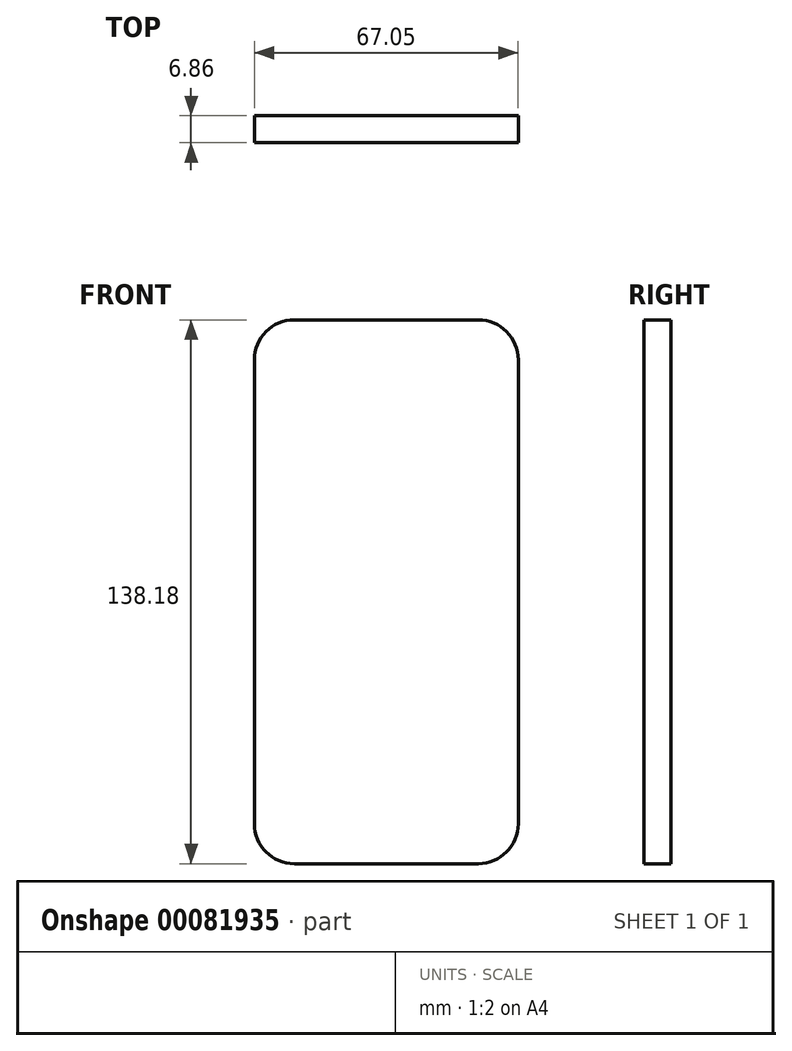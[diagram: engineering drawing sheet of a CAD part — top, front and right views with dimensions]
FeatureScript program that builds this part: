
annotation { "Feature Type Name" : "Feature", "Feature Type Description" : "" }
export const myFeature = defineFeature(function(context is Context, id is Id, definition is map)
    precondition{}
    {
        {
            var Q0;
            Q0=qCreatedBy(makeId("Front.planeOp"),FACE);
            var sketch = newSketch(context, id + "F0", { "sketchPlane" : qUnion([Q0])});
            skLineSegment(sketch, "E0.bottom", {"start": v(-37.54, 72.42) * mm, "end": v(29.51, 72.42) * mm});
            skLineSegment(sketch, "E0.top", {"start": v(-37.54, -65.76) * mm, "end": v(29.51, -65.76) * mm});
            skLineSegment(sketch, "E0.left", {"start": v(-37.54, 72.42) * mm, "end": v(-37.54, -65.76) * mm});
            skLineSegment(sketch, "E0.right", {"start": v(29.51, 72.42) * mm, "end": v(29.51, -65.76) * mm});
            skSolve(sketch);
        }
        {
            var Q0;
            Q0=makeQuery(id+"F0.imprint","IMPRINT",FACE,{"disambiguationData":[TD([[makeQuery(id+"F0.imprint","IMPRINT",EDGE,{"derivedFrom":sQuery(id+"F0.wireOp",EDGE,"E0.bottom")}),-1.0]])]});
            extrude(context, id + "F1", {"entities" : qUnion([Q0]), "depth" : 6.86 * mm});
        }
        {
            var Q0;
            Q0=makeQuery(id+"F1.opExtrude","SWEPT_EDGE",EDGE,{"disambiguationData":[OSD([sQuery(id+"F0.wireOp",EDGE,"E0.bottom"),sQuery(id+"F0.wireOp",EDGE,"E0.right")])]});
            var Q1;
            Q1=makeQuery(id+"F1.opExtrude","SWEPT_EDGE",EDGE,{"disambiguationData":[OSD([sQuery(id+"F0.wireOp",EDGE,"E0.top"),sQuery(id+"F0.wireOp",EDGE,"E0.right")])]});
            var Q2;
            Q2=makeQuery(id+"F1.opExtrude","SWEPT_EDGE",EDGE,{"disambiguationData":[OSD([sQuery(id+"F0.wireOp",EDGE,"E0.top"),sQuery(id+"F0.wireOp",EDGE,"E0.left")])]});
            var Q3;
            Q3=makeQuery(id+"F1.opExtrude","SWEPT_EDGE",EDGE,{"disambiguationData":[OSD([sQuery(id+"F0.wireOp",EDGE,"E0.bottom"),sQuery(id+"F0.wireOp",EDGE,"E0.left")])]});
            fillet(context, id + "F2", {"entities" : qUnion([Q0, Q1, Q2, Q3]), "radius" : 10.16 * mm, "tangentPropagation" : true, "allowEdgeOverflow" : false});
        }
    });
